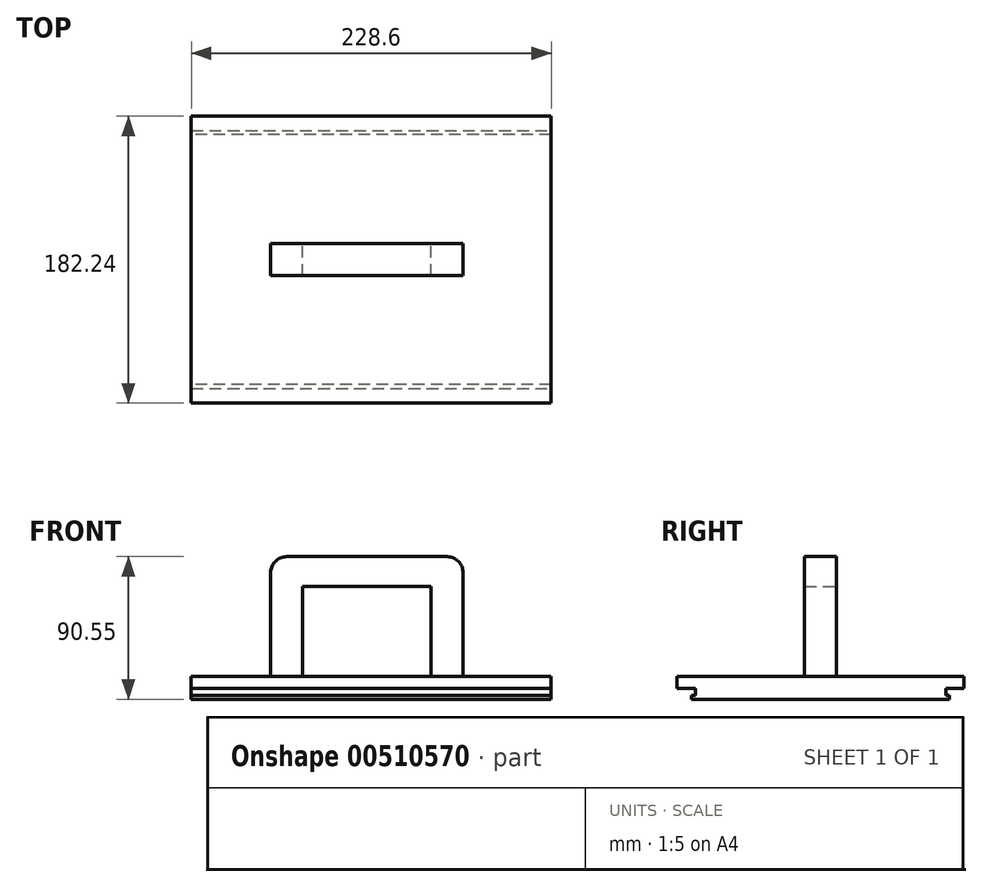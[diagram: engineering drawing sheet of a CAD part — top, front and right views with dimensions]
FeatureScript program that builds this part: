
annotation { "Feature Type Name" : "Feature", "Feature Type Description" : "" }
export const myFeature = defineFeature(function(context is Context, id is Id, definition is map)
    precondition{}
    {
        {
            var Q0;
            Q0=qCreatedBy(makeId("Top.planeOp"),FACE);
            var sketch = newSketch(context, id + "F0", { "sketchPlane" : qUnion([Q0])});
            skLineSegment(sketch, "E0.bottom", {"start": v(-60.55, -52.33) * mm, "end": v(168.05, -52.33) * mm});
            skLineSegment(sketch, "E0.top", {"start": v(-60.55, 129.91) * mm, "end": v(168.05, 129.91) * mm});
            skLineSegment(sketch, "E0.left", {"start": v(-60.55, -52.33) * mm, "end": v(-60.55, 129.91) * mm});
            skLineSegment(sketch, "E0.right", {"start": v(168.05, -52.33) * mm, "end": v(168.05, 129.91) * mm});
            skSolve(sketch);
        }
        {
            var Q0;
            Q0=makeQuery(id+"F0.imprint","IMPRINT",FACE,{"disambiguationData":[TD([[makeQuery(id+"F0.imprint","IMPRINT",EDGE,{"derivedFrom":sQuery(id+"F0.wireOp",EDGE,"E0.bottom")}),1.0]])]});
            extrude(context, id + "F1", {"entities" : qUnion([Q0]), "depth" : 7.62 * mm, "offsetDistance" : 25.4 * mm});
        }
        {
            var Q0;
            Q0=makeQuery(id+"F1.opExtrude","CAP_FACE",FACE,{"disambiguationData":[OSD([sQuery(id+"F0.wireOp",EDGE,"E0.bottom"),sQuery(id+"F0.wireOp",EDGE,"E0.top"),sQuery(id+"F0.wireOp",EDGE,"E0.left"),sQuery(id+"F0.wireOp",EDGE,"E0.right")])],"isStart":true});
            var sketch = newSketch(context, id + "F2", { "sketchPlane" : qUnion([Q0])});
            skLineSegment(sketch, "E1", {"start": v(168.05, 52.33) * mm, "end": v(168.05, 40.6) * mm, "construction": true});
            skLineSegment(sketch, "E2", {"start": v(168.05, -129.91) * mm, "end": v(168.05, -118.18) * mm, "construction": true});
            skLineSegment(sketch, "E3.bottom", {"start": v(168.05, 40.6) * mm, "end": v(-60.55, 40.6) * mm});
            skLineSegment(sketch, "E3.top", {"start": v(168.05, -118.18) * mm, "end": v(-60.55, -118.18) * mm});
            skLineSegment(sketch, "E3.left", {"start": v(168.05, 40.6) * mm, "end": v(168.05, -118.18) * mm});
            skLineSegment(sketch, "E3.right", {"start": v(-60.55, 40.6) * mm, "end": v(-60.55, -118.18) * mm});
            skSolve(sketch);
        }
        {
            var Q0;
            Q0 = qSketchRegion(id + "F2", true);
            extrude(context, id + "F3", {"entities" : qUnion([Q0]), "operationType" : NewBodyOperationType.ADD, "depth" : 6.73 * mm, "offsetDistance" : 25.4 * mm});
        }
        {
            var Q0;
            Q0=makeQuery(id+"F3.boolean.opBoolean","MERGE",FACE,{"derivedFrom":[makeQuery(id+"F1.opExtrude","SWEPT_FACE",FACE,{"disambiguationData":[OSD([sQuery(id+"F0.wireOp",EDGE,"E0.right")])]}),makeQuery(id+"F3.opExtrude","SWEPT_FACE",FACE,{"disambiguationData":[OSD([sQuery(id+"F2.wireOp",EDGE,"E3.left")])]})]});
            var sketch = newSketch(context, id + "F4", { "sketchPlane" : qUnion([Q0])});
            skLineSegment(sketch, "E4.bottom", {"start": v(118.18, -6.73) * mm, "end": v(120.72, -6.73) * mm});
            skLineSegment(sketch, "E4.top", {"start": v(118.18, -4.2) * mm, "end": v(120.72, -4.2) * mm});
            skLineSegment(sketch, "E4.left", {"start": v(118.18, -6.73) * mm, "end": v(118.18, -4.2) * mm});
            skLineSegment(sketch, "E4.right", {"start": v(120.72, -6.73) * mm, "end": v(120.72, -4.2) * mm});
            skLineSegment(sketch, "E5.bottom", {"start": v(-40.6, -6.73) * mm, "end": v(-43.14, -6.73) * mm});
            skLineSegment(sketch, "E5.top", {"start": v(-40.6, -4.2) * mm, "end": v(-43.14, -4.2) * mm});
            skLineSegment(sketch, "E5.left", {"start": v(-40.6, -6.73) * mm, "end": v(-40.6, -4.2) * mm});
            skLineSegment(sketch, "E5.right", {"start": v(-43.14, -6.73) * mm, "end": v(-43.14, -4.2) * mm});
            skSolve(sketch);
        }
        {
            var Q0;
            Q0 = qSketchRegion(id + "F4", true);
            extrude(context, id + "F5", {"entities" : qUnion([Q0]), "operationType" : NewBodyOperationType.ADD, "oppositeDirection" : true, "depth" : 228.6 * mm, "offsetDistance" : 25.4 * mm});
        }
        {
            var Q0;
            Q0=makeQuery(id+"F1.opExtrude","CAP_FACE",FACE,{"disambiguationData":[OSD([sQuery(id+"F0.wireOp",EDGE,"E0.bottom"),sQuery(id+"F0.wireOp",EDGE,"E0.top"),sQuery(id+"F0.wireOp",EDGE,"E0.left"),sQuery(id+"F0.wireOp",EDGE,"E0.right")])],"isStart":false});
            var sketch = newSketch(context, id + "F6", { "sketchPlane" : qUnion([Q0])});
            skPoint(sketch, "E6.middle", {"position": v(101.9, 30.09) * mm});
            skLineSegment(sketch, "E7.bottom", {"start": v(10.16, 28.63) * mm, "end": v(-10.16, 28.63) * mm});
            skLineSegment(sketch, "E7.top", {"start": v(10.16, 48.95) * mm, "end": v(-10.16, 48.95) * mm});
            skLineSegment(sketch, "E7.left", {"start": v(10.16, 28.63) * mm, "end": v(10.16, 48.95) * mm});
            skLineSegment(sketch, "E7.right", {"start": v(-10.16, 28.63) * mm, "end": v(-10.16, 48.95) * mm});
            skPoint(sketch, "E7.middle", {"position": v(0, 38.79) * mm});
            skLineSegment(sketch, "E8", {"start": v(91.73, 48.95) * mm, "end": v(101.9, 48.95) * mm});
            skLineSegment(sketch, "E9", {"start": v(101.9, 48.95) * mm, "end": v(112.05, 48.95) * mm});
            skLineSegment(sketch, "E10", {"start": v(112.05, 48.95) * mm, "end": v(112.05, 28.63) * mm});
            skLineSegment(sketch, "E11", {"start": v(112.05, 28.63) * mm, "end": v(91.73, 28.63) * mm});
            skLineSegment(sketch, "E12", {"start": v(91.73, 28.63) * mm, "end": v(91.73, 48.95) * mm});
            skSolve(sketch);
        }
        {
            var Q0;
            Q0 = qSketchRegion(id + "F6", true);
            extrude(context, id + "F7", {"entities" : qUnion([Q0]), "operationType" : NewBodyOperationType.ADD, "depth" : 76.2 * mm, "offsetDistance" : 25.4 * mm});
        }
        {
            var Q0;
            Q0=makeQuery(id+"F7.opExtrude","CAP_FACE",FACE,{"disambiguationData":[OSD([sQuery(id+"F6.wireOp",EDGE,"E7.bottom"),sQuery(id+"F6.wireOp",EDGE,"E7.top"),sQuery(id+"F6.wireOp",EDGE,"E7.left"),sQuery(id+"F6.wireOp",EDGE,"E7.right")])],"isStart":false});
            var sketch = newSketch(context, id + "F8", { "sketchPlane" : qUnion([Q0])});
            skLineSegment(sketch, "E13.bottom", {"start": v(10.16, 28.63) * mm, "end": v(91.73, 28.63) * mm});
            skLineSegment(sketch, "E13.top", {"start": v(10.16, 48.95) * mm, "end": v(91.73, 48.95) * mm});
            skLineSegment(sketch, "E13.left", {"start": v(10.16, 28.63) * mm, "end": v(10.16, 48.95) * mm});
            skLineSegment(sketch, "E13.right", {"start": v(91.73, 28.63) * mm, "end": v(91.73, 48.95) * mm});
            skSolve(sketch);
        }
        {
            var Q0;
            Q0 = qSketchRegion(id + "F8", true);
            extrude(context, id + "F9", {"entities" : qUnion([Q0]), "operationType" : NewBodyOperationType.ADD, "oppositeDirection" : true, "depth" : 19.05 * mm, "offsetDistance" : 25.4 * mm});
        }
        {
            var Q0;
            Q0=makeQuery(id+"F7.opExtrude","CAP_EDGE",EDGE,{"disambiguationData":[OSD([sQuery(id+"F6.wireOp",EDGE,"E7.right")])],"isStart":false});
            var Q1;
            Q1=makeQuery(id+"F7.opExtrude","CAP_EDGE",EDGE,{"disambiguationData":[OSD([sQuery(id+"F6.wireOp",EDGE,"E10")])],"isStart":false});
            var Q2;
            Q2=makeQuery(id+"F9.opExtrude","CAP_EDGE",EDGE,{"disambiguationData":[OSD([sQuery(id+"F8.wireOp",EDGE,"E13.left")])],"isStart":false});
            var Q3;
            Q3=makeQuery(id+"F9.opExtrude","CAP_EDGE",EDGE,{"disambiguationData":[OSD([sQuery(id+"F8.wireOp",EDGE,"E13.right")])],"isStart":false});
            fillet(context, id + "F10", {"entities" : qUnion([Q0, Q1, Q2, Q3]), "radius" : 10.16 * mm, "tangentPropagation" : true, "allowEdgeOverflow" : false});
        }
    });
